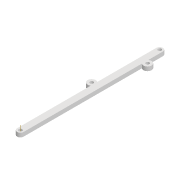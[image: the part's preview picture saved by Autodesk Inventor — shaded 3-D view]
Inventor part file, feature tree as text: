
AUTODESK INVENTOR PART (.ipt)
format: ipt  version: 2022 (Build 260153000, 153)  size: 106,496 bytes
history: native  units: mm
features: extrude x1, other x1, sketch x1
ambient origin geometry x8: Origin, YZ Plane, XZ Plane, XY Plane, X Axis, Y Axis, Z Axis, Center Point
bodies: Solid1 (feature_tree)
feature tree (3):
  extrude  "Extrusion1"  Depth=8.0mm
  other  "Work Axis1"
  sketch  "Sketch1"  dims[d0=172.0mm d1=8.0mm d2=4.2mm d3=4.2mm d4=5.0mm d5=0.0mm d8=4.2mm d9=93.0mm d10=3.0mm d11=10.0mm d12=4.2mm d13=10.0mm d15=3.0mm d16=150.0mm]
